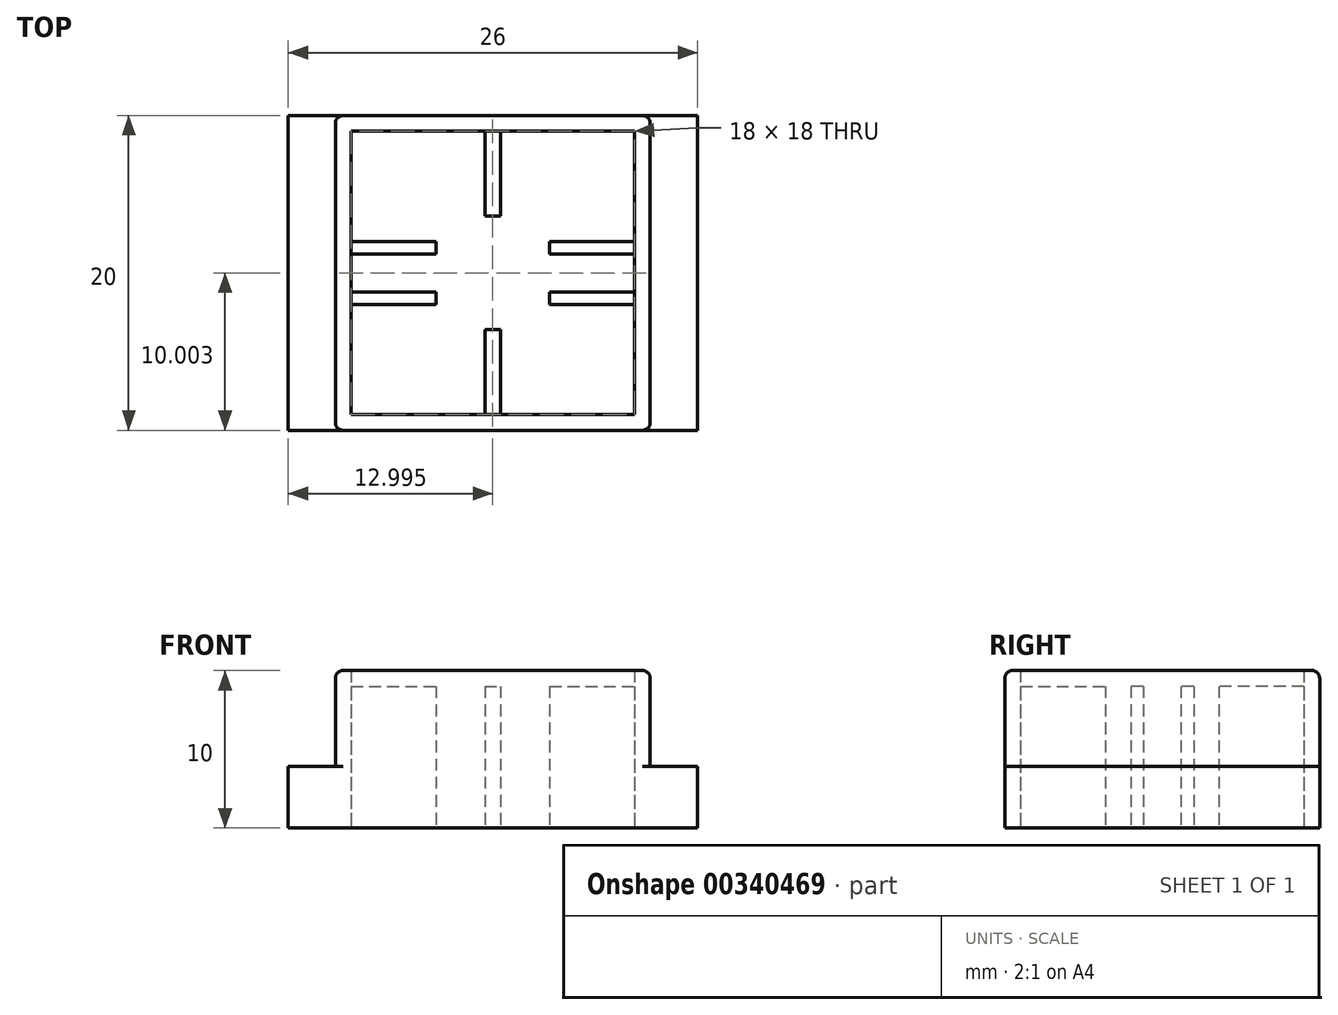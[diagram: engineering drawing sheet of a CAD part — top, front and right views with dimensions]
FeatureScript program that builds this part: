
annotation { "Feature Type Name" : "Feature", "Feature Type Description" : "" }
export const myFeature = defineFeature(function(context is Context, id is Id, definition is map)
    precondition{}
    {
        {
            var Q0;
            Q0=qCreatedBy(makeId("Top.planeOp"),FACE);
            var sketch = newSketch(context, id + "F0", { "sketchPlane" : qUnion([Q0])});
            skLineSegment(sketch, "E0.bottom", {"start": v(-88.88, 8.7) * mm, "end": v(-68.88, 8.7) * mm});
            skLineSegment(sketch, "E0.top", {"start": v(-88.88, -11.3) * mm, "end": v(-68.88, -11.3) * mm});
            skLineSegment(sketch, "E0.left", {"start": v(-88.88, 8.7) * mm, "end": v(-88.88, -11.3) * mm});
            skLineSegment(sketch, "E0.right", {"start": v(-68.88, 8.7) * mm, "end": v(-68.88, -11.3) * mm});
            skSolve(sketch);
        }
        {
            var Q0;
            Q0=makeQuery(id+"F0.imprint","IMPRINT",FACE,{"disambiguationData":[TD([[makeQuery(id+"F0.imprint","IMPRINT",EDGE,{"derivedFrom":sQuery(id+"F0.wireOp",EDGE,"E0.bottom")}),-1.0]])]});
            extrude(context, id + "F1", {"entities" : qUnion([Q0]), "depth" : 10 * mm});
        }
        {
            var Q0;
            Q0=makeQuery(id+"F6.boolean.opBoolean","MERGE",FACE,{"derivedFrom":[makeQuery(id+"F1.opExtrude","CAP_FACE",FACE,{"disambiguationData":[OSD([sQuery(id+"F0.wireOp",EDGE,"E0.bottom"),sQuery(id+"F0.wireOp",EDGE,"E0.top"),sQuery(id+"F0.wireOp",EDGE,"E0.left"),sQuery(id+"F0.wireOp",EDGE,"E0.right")])],"isStart":true}),makeQuery(id+"F6.opExtrude","CAP_FACE",FACE,{"disambiguationData":[OSD([sQuery(id+"F5.wireOp",EDGE,"E8.bottom"),sQuery(id+"F5.wireOp",EDGE,"E8.top"),sQuery(id+"F5.wireOp",EDGE,"E8.left"),sQuery(id+"F5.wireOp",EDGE,"E8.right"),sQuery(id+"F5.wireOp",EDGE,"E9.trimOffspring"),sQuery(id+"F5.wireOp",EDGE,"E11.trimOffspring"),sQuery(id+"F5.wireOp",EDGE,"E13"),sQuery(id+"F5.wireOp",EDGE,"E14"),sQuery(id+"F5.wireOp",EDGE,"E15.bottom"),sQuery(id+"F5.wireOp",EDGE,"E15.top"),sQuery(id+"F5.wireOp",EDGE,"E15.left"),sQuery(id+"F5.wireOp",EDGE,"E16.bottom"),sQuery(id+"F5.wireOp",EDGE,"E16.top"),sQuery(id+"F5.wireOp",EDGE,"E16.left"),sQuery(id+"F5.wireOp",EDGE,"E17.bottom"),sQuery(id+"F5.wireOp",EDGE,"E17.top"),sQuery(id+"F5.wireOp",EDGE,"E17.right"),sQuery(id+"F5.wireOp",EDGE,"E18.bottom"),sQuery(id+"F5.wireOp",EDGE,"E18.top"),sQuery(id+"F5.wireOp",EDGE,"E18.right")])],"isStart":true})]});
            var sketch = newSketch(context, id + "F2", { "sketchPlane" : qUnion([Q0])});
            skLineSegment(sketch, "E1.bottom", {"start": v(-88.88, 11.3) * mm, "end": v(-68.88, 11.3) * mm});
            skLineSegment(sketch, "E1.top", {"start": v(-88.88, 14.3) * mm, "end": v(-68.88, 14.3) * mm, "construction": true});
            skLineSegment(sketch, "E1.left", {"start": v(-88.88, 11.3) * mm, "end": v(-88.88, 14.3) * mm, "construction": true});
            skLineSegment(sketch, "E1.right", {"start": v(-68.88, 11.3) * mm, "end": v(-68.88, 14.3) * mm, "construction": true});
            skLineSegment(sketch, "E2.bottom", {"start": v(-88.88, -8.7) * mm, "end": v(-68.88, -8.7) * mm});
            skLineSegment(sketch, "E2.top", {"start": v(-88.88, -11.7) * mm, "end": v(-68.88, -11.7) * mm});
            skLineSegment(sketch, "E2.left", {"start": v(-88.88, -8.7) * mm, "end": v(-88.88, -11.7) * mm, "construction": true});
            skLineSegment(sketch, "E2.right", {"start": v(-68.88, -8.7) * mm, "end": v(-68.88, -11.7) * mm, "construction": true});
            skLineSegment(sketch, "E3.bottom", {"start": v(-88.88, -8.7) * mm, "end": v(-91.88, -8.7) * mm});
            skLineSegment(sketch, "E3.top", {"start": v(-88.88, 11.3) * mm, "end": v(-91.88, 11.3) * mm});
            skLineSegment(sketch, "E3.left", {"start": v(-88.88, -8.7) * mm, "end": v(-88.88, 11.3) * mm});
            skLineSegment(sketch, "E3.right", {"start": v(-91.88, -8.7) * mm, "end": v(-91.88, 11.3) * mm});
            skLineSegment(sketch, "E4.bottom", {"start": v(-68.88, -8.7) * mm, "end": v(-65.88, -8.7) * mm});
            skLineSegment(sketch, "E4.top", {"start": v(-68.88, 11.3) * mm, "end": v(-65.88, 11.3) * mm});
            skLineSegment(sketch, "E4.left", {"start": v(-68.88, -8.7) * mm, "end": v(-68.88, 11.3) * mm});
            skLineSegment(sketch, "E4.right", {"start": v(-65.88, -8.7) * mm, "end": v(-65.88, 11.3) * mm});
            skLineSegment(sketch, "E5.bottom", {"start": v(-88.88, -11.7) * mm, "end": v(-68.88, -11.7) * mm, "construction": true});
            skLineSegment(sketch, "E5.top", {"start": v(-88.88, -16.7) * mm, "end": v(-68.88, -16.7) * mm, "construction": true});
            skLineSegment(sketch, "E5.left", {"start": v(-88.88, -11.7) * mm, "end": v(-88.88, -16.7) * mm, "construction": true});
            skLineSegment(sketch, "E5.right", {"start": v(-68.88, -11.7) * mm, "end": v(-68.88, -16.7) * mm, "construction": true});
            skCircle(sketch, "E6", {"center": v(-78.88, -13.7) * mm, "radius": 1.5 * mm, "construction": true});
            skSolve(sketch);
        }
        {
            var Q0;
            Q0=qSketchRegion(id+"F2",true);
            extrude(context, id + "F3", {"entities" : qUnion([Q0]), "operationType" : NewBodyOperationType.ADD, "oppositeDirection" : true, "depth" : 0.95 * mm});
        }
        {
            var Q0;
            Q0=makeQuery(id+"F1.opExtrude","CAP_FACE",FACE,{"disambiguationData":[OSD([sQuery(id+"F0.wireOp",EDGE,"E0.bottom"),sQuery(id+"F0.wireOp",EDGE,"E0.top"),sQuery(id+"F0.wireOp",EDGE,"E0.left"),sQuery(id+"F0.wireOp",EDGE,"E0.right")])],"isStart":true});
            shell(context, id + "F4", {"entities" : qUnion([Q0]), "thickness" : 1 * mm});
        }
        {
            var Q0;
            Q0=qCreatedBy(makeId("Top.planeOp"),FACE);
            var sketch = newSketch(context, id + "F5", { "sketchPlane" : qUnion([Q0])});
            skLineSegment(sketch, "E7.bottom", {"start": v(-87.88, -0.1) * mm, "end": v(-79.38, -0.1) * mm, "construction": true});
            skLineSegment(sketch, "E7.top", {"start": v(-87.88, -2.5) * mm, "end": v(-79.38, -2.5) * mm, "construction": true});
            skLineSegment(sketch, "E7.left", {"start": v(-87.88, -0.1) * mm, "end": v(-87.88, -2.5) * mm, "construction": true});
            skLineSegment(sketch, "E7.right", {"start": v(-69.88, -0.1) * mm, "end": v(-69.88, -2.5) * mm, "construction": true});
            skLineSegment(sketch, "E8.bottom", {"start": v(-79.38, 7.7) * mm, "end": v(-78.38, 7.7) * mm});
            skLineSegment(sketch, "E8.top", {"start": v(-79.38, -10.3) * mm, "end": v(-78.38, -10.3) * mm});
            skLineSegment(sketch, "E8.left", {"start": v(-79.38, 7.7) * mm, "end": v(-79.38, -0.1) * mm});
            skLineSegment(sketch, "E8.right", {"start": v(-78.38, 7.7) * mm, "end": v(-78.38, -0.1) * mm});
            skLineSegment(sketch, "E9.trimOffspring", {"start": v(-79.38, -10.3) * mm, "end": v(-79.38, -2.5) * mm});
            skLineSegment(sketch, "E10.trimOffspring", {"start": v(-78.38, -0.1) * mm, "end": v(-69.88, -0.1) * mm, "construction": true});
            skLineSegment(sketch, "E11.trimOffspring", {"start": v(-78.38, -2.5) * mm, "end": v(-78.38, -10.3) * mm});
            skLineSegment(sketch, "E12.trimOffspring", {"start": v(-78.38, -2.5) * mm, "end": v(-69.88, -2.5) * mm, "construction": true});
            skLineSegment(sketch, "E13", {"start": v(-79.38, -2.5) * mm, "end": v(-79.38, -0.1) * mm});
            skLineSegment(sketch, "E14", {"start": v(-78.38, -2.5) * mm, "end": v(-78.38, -0.1) * mm});
            skLineSegment(sketch, "E15.bottom", {"start": v(-87.88, -2.5) * mm, "end": v(-79.38, -2.5) * mm});
            skLineSegment(sketch, "E15.top", {"start": v(-87.88, -3.3) * mm, "end": v(-79.38, -3.3) * mm});
            skLineSegment(sketch, "E15.left", {"start": v(-87.88, -2.5) * mm, "end": v(-87.88, -3.3) * mm});
            skLineSegment(sketch, "E15.right", {"start": v(-79.38, -2.5) * mm, "end": v(-79.38, -3.3) * mm});
            skLineSegment(sketch, "E16.bottom", {"start": v(-87.88, -0.1) * mm, "end": v(-79.38, -0.1) * mm});
            skLineSegment(sketch, "E16.top", {"start": v(-87.88, 0.7) * mm, "end": v(-79.38, 0.7) * mm});
            skLineSegment(sketch, "E16.left", {"start": v(-87.88, -0.1) * mm, "end": v(-87.88, 0.7) * mm});
            skLineSegment(sketch, "E16.right", {"start": v(-79.38, -0.1) * mm, "end": v(-79.38, 0.7) * mm});
            skLineSegment(sketch, "E17.bottom", {"start": v(-78.38, -3.3) * mm, "end": v(-69.88, -3.3) * mm});
            skLineSegment(sketch, "E17.top", {"start": v(-78.38, -2.5) * mm, "end": v(-69.88, -2.5) * mm});
            skLineSegment(sketch, "E17.left", {"start": v(-78.38, -3.3) * mm, "end": v(-78.38, -2.5) * mm});
            skLineSegment(sketch, "E17.right", {"start": v(-69.88, -3.3) * mm, "end": v(-69.88, -2.5) * mm});
            skLineSegment(sketch, "E18.bottom", {"start": v(-78.38, -0.1) * mm, "end": v(-69.88, -0.1) * mm});
            skLineSegment(sketch, "E18.top", {"start": v(-78.38, 0.7) * mm, "end": v(-69.88, 0.7) * mm});
            skLineSegment(sketch, "E18.left", {"start": v(-78.38, -0.1) * mm, "end": v(-78.38, 0.7) * mm});
            skLineSegment(sketch, "E18.right", {"start": v(-69.88, -0.1) * mm, "end": v(-69.88, 0.7) * mm});
            skSolve(sketch);
        }
        {
            var Q0;
            Q0=makeQuery(id+"F5.imprint","IMPRINT",FACE,{"disambiguationData":[TD([[makeQuery(id+"F5.imprint","IMPRINT",EDGE,{"derivedFrom":sQuery(id+"F5.wireOp",EDGE,"E8.bottom")}),-1.0]])]});
            var Q1;
            Q1=makeQuery(id+"F5.imprint","IMPRINT",FACE,{"disambiguationData":[TD([[makeQuery(id+"F5.imprint","IMPRINT",EDGE,{"derivedFrom":sQuery(id+"F5.wireOp",EDGE,"E15.bottom")}),-1.0]])]});
            var Q2;
            Q2=makeQuery(id+"F5.imprint","IMPRINT",FACE,{"disambiguationData":[TD([[makeQuery(id+"F5.imprint","IMPRINT",EDGE,{"derivedFrom":sQuery(id+"F5.wireOp",EDGE,"E16.bottom")}),1.0]])]});
            var Q3;
            Q3=makeQuery(id+"F5.imprint","IMPRINT",FACE,{"disambiguationData":[TD([[makeQuery(id+"F5.imprint","IMPRINT",EDGE,{"derivedFrom":sQuery(id+"F5.wireOp",EDGE,"E18.bottom")}),1.0]])]});
            var Q4;
            Q4=makeQuery(id+"F5.imprint","IMPRINT",FACE,{"disambiguationData":[TD([[makeQuery(id+"F5.imprint","IMPRINT",EDGE,{"derivedFrom":sQuery(id+"F5.wireOp",EDGE,"E17.bottom")}),1.0]])]});
            var Q5;
            Q5=sQuery(id+"F5.wireOp",EDGE,"E8.left");
            var Q6;
            Q6=sQuery(id+"F5.wireOp",EDGE,"E9.trimOffspring");
            var Q7;
            Q7=sQuery(id+"F5.wireOp",EDGE,"E7.top");
            var Q8;
            Q8=sQuery(id+"F5.wireOp",EDGE,"E10.trimOffspring");
            var Q9;
            Q9=sQuery(id+"F5.wireOp",EDGE,"E8.bottom");
            var Q10;
            Q10=sQuery(id+"F5.wireOp",EDGE,"E8.right");
            var Q11;
            Q11=sQuery(id+"F5.wireOp",EDGE,"E8.top");
            var Q12;
            Q12=sQuery(id+"F5.wireOp",EDGE,"E7.bottom");
            var Q13;
            Q13=sQuery(id+"F5.wireOp",EDGE,"E11.trimOffspring");
            var Q14;
            Q14=sQuery(id+"F5.wireOp",EDGE,"E12.trimOffspring");
            var Q15;
            Q15=sQuery(id+"F5.wireOp",EDGE,"E7.right");
            var Q16;
            Q16=sQuery(id+"F5.wireOp",EDGE,"E7.left");
            extrude(context, id + "F6", {"entities" : qUnion([Q0, Q1, Q2, Q3, Q4]), "operationType" : NewBodyOperationType.ADD, "surfaceEntities" : qUnion([Q5, Q6, Q7, Q8, Q9, Q10, Q11, Q12, Q13, Q14, Q15, Q16]), "depth" : 9 * mm});
        }
        {
            var Q0;
            Q0=makeQuery(id+"F6.boolean.opBoolean","MERGE",FACE,{"derivedFrom":[makeQuery(id+"F1.opExtrude","CAP_FACE",FACE,{"disambiguationData":[OSD([sQuery(id+"F0.wireOp",EDGE,"E0.bottom"),sQuery(id+"F0.wireOp",EDGE,"E0.top"),sQuery(id+"F0.wireOp",EDGE,"E0.left"),sQuery(id+"F0.wireOp",EDGE,"E0.right")])],"isStart":true}),makeQuery(id+"F6.opExtrude","CAP_FACE",FACE,{"disambiguationData":[OSD([sQuery(id+"F5.wireOp",EDGE,"E7.bottom"),sQuery(id+"F5.wireOp",EDGE,"E7.top"),sQuery(id+"F5.wireOp",EDGE,"E7.left"),sQuery(id+"F5.wireOp",EDGE,"E7.right"),sQuery(id+"F5.wireOp",EDGE,"E8.bottom"),sQuery(id+"F5.wireOp",EDGE,"E8.top"),sQuery(id+"F5.wireOp",EDGE,"E8.left"),sQuery(id+"F5.wireOp",EDGE,"E8.right"),sQuery(id+"F5.wireOp",EDGE,"E9.trimOffspring"),sQuery(id+"F5.wireOp",EDGE,"E10.trimOffspring"),sQuery(id+"F5.wireOp",EDGE,"E11.trimOffspring"),sQuery(id+"F5.wireOp",EDGE,"E12.trimOffspring")])],"isStart":true})]});
            var sketch = newSketch(context, id + "F7", { "sketchPlane" : qUnion([Q0])});
            skLineSegment(sketch, "E19.bottom", {"start": v(-75.28, -2.3) * mm, "end": v(-82.48, -2.3) * mm});
            skLineSegment(sketch, "E19.top", {"start": v(-75.28, 4.9) * mm, "end": v(-82.48, 4.9) * mm});
            skLineSegment(sketch, "E19.left", {"start": v(-75.28, -2.3) * mm, "end": v(-75.28, 4.9) * mm});
            skLineSegment(sketch, "E19.right", {"start": v(-82.48, -2.3) * mm, "end": v(-82.48, 4.9) * mm});
            skPoint(sketch, "E19.middle.positionSnap1", {"position": v(-88.88, 1.8) * mm});
            skSolve(sketch);
        }
        {
            var Q0;
            {var subQ1=makeQuery(id+"F6.opExtrude","CAP_EDGE",EDGE,{"disambiguationData":[OSD([sQuery(id+"F5.wireOp",EDGE,"E8.right")])],"isStart":true});var subQ3=sQuery(id+"F7.wireOp",EDGE,"E19.bottom");var subQ4=makeQuery(id+"F7.imprint","INTERSECT",VERTEX,{"derivedFrom":[subQ1,subQ3]});Q0=makeQuery(id+"F7.imprint","IMPRINT",FACE,{"disambiguationData":[TD([[makeQuery(id+"F7.imprint","IMPRINT",EDGE,{"disambiguationData":[TD([[subQ4,-1.0]])],"derivedFrom":subQ3}),-1.0]])]});}
            extrude(context, id + "F8", {"entities" : qUnion([Q0]), "operationType" : NewBodyOperationType.REMOVE, "oppositeDirection" : true, "depth" : 9 * mm});
        }
        {
            var Q0;
            Q0=makeQuery(id+"F1.opExtrude","SWEPT_EDGE",EDGE,{"disambiguationData":[OSD([sQuery(id+"F0.wireOp",EDGE,"E0.top"),sQuery(id+"F0.wireOp",EDGE,"E0.right")])]});
            var Q1;
            Q1=makeQuery(id+"F1.opExtrude","CAP_EDGE",EDGE,{"disambiguationData":[OSD([sQuery(id+"F0.wireOp",EDGE,"E0.top")])],"isStart":false});
            var Q2;
            Q2=makeQuery(id+"F1.opExtrude","CAP_EDGE",EDGE,{"disambiguationData":[OSD([sQuery(id+"F0.wireOp",EDGE,"E0.right")])],"isStart":false});
            var Q3;
            Q3=makeQuery(id+"F1.opExtrude","SWEPT_EDGE",EDGE,{"disambiguationData":[OSD([sQuery(id+"F0.wireOp",EDGE,"E0.bottom"),sQuery(id+"F0.wireOp",EDGE,"E0.right")])]});
            var Q4;
            Q4=makeQuery(id+"F1.opExtrude","CAP_EDGE",EDGE,{"disambiguationData":[OSD([sQuery(id+"F0.wireOp",EDGE,"E0.bottom")])],"isStart":false});
            var Q5;
            Q5=makeQuery(id+"F1.opExtrude","SWEPT_EDGE",EDGE,{"disambiguationData":[OSD([sQuery(id+"F0.wireOp",EDGE,"E0.bottom"),sQuery(id+"F0.wireOp",EDGE,"E0.left")])]});
            var Q6;
            Q6=makeQuery(id+"F1.opExtrude","CAP_EDGE",EDGE,{"disambiguationData":[OSD([sQuery(id+"F0.wireOp",EDGE,"E0.left")])],"isStart":false});
            var Q7;
            Q7=makeQuery(id+"F1.opExtrude","SWEPT_EDGE",EDGE,{"disambiguationData":[OSD([sQuery(id+"F0.wireOp",EDGE,"E0.top"),sQuery(id+"F0.wireOp",EDGE,"E0.left")])]});
            var Q8;
            Q8=makeQuery(id+"FdcNGCSEVtLFmFF_0.opExtrude","SWEPT_EDGE",EDGE,{"disambiguationData":[OSD([sQuery(id+"FRnwog6KuLiXbKg_0.wireOp",EDGE,"NmKWu525-oT8c-AXwx-9Qw7-ty39SNDPMHe7.bottom"),sQuery(id+"FRnwog6KuLiXbKg_0.wireOp",EDGE,"NmKWu525-oT8c-AXwx-9Qw7-ty39SNDPMHe7.right")])]});
            var Q9;
            Q9=makeQuery(id+"FdcNGCSEVtLFmFF_0.opExtrude","CAP_EDGE",EDGE,{"disambiguationData":[OSD([sQuery(id+"FRnwog6KuLiXbKg_0.wireOp",EDGE,"NmKWu525-oT8c-AXwx-9Qw7-ty39SNDPMHe7.bottom")])],"isStart":false});
            var Q10;
            Q10=makeQuery(id+"FdcNGCSEVtLFmFF_0.opExtrude","SWEPT_EDGE",EDGE,{"disambiguationData":[OSD([sQuery(id+"FRnwog6KuLiXbKg_0.wireOp",EDGE,"NmKWu525-oT8c-AXwx-9Qw7-ty39SNDPMHe7.bottom"),sQuery(id+"FRnwog6KuLiXbKg_0.wireOp",EDGE,"NmKWu525-oT8c-AXwx-9Qw7-ty39SNDPMHe7.left")])]});
            var Q11;
            Q11=makeQuery(id+"FdcNGCSEVtLFmFF_0.opExtrude","CAP_EDGE",EDGE,{"disambiguationData":[OSD([sQuery(id+"FRnwog6KuLiXbKg_0.wireOp",EDGE,"NmKWu525-oT8c-AXwx-9Qw7-ty39SNDPMHe7.right")])],"isStart":false});
            var Q12;
            Q12=makeQuery(id+"FdcNGCSEVtLFmFF_0.opExtrude","SWEPT_EDGE",EDGE,{"disambiguationData":[OSD([sQuery(id+"FRnwog6KuLiXbKg_0.wireOp",EDGE,"NmKWu525-oT8c-AXwx-9Qw7-ty39SNDPMHe7.top"),sQuery(id+"FRnwog6KuLiXbKg_0.wireOp",EDGE,"NmKWu525-oT8c-AXwx-9Qw7-ty39SNDPMHe7.right")])]});
            var Q13;
            Q13=makeQuery(id+"FdcNGCSEVtLFmFF_0.opExtrude","CAP_EDGE",EDGE,{"disambiguationData":[OSD([sQuery(id+"FRnwog6KuLiXbKg_0.wireOp",EDGE,"NmKWu525-oT8c-AXwx-9Qw7-ty39SNDPMHe7.top")])],"isStart":false});
            var Q14;
            Q14=makeQuery(id+"FdcNGCSEVtLFmFF_0.opExtrude","SWEPT_EDGE",EDGE,{"disambiguationData":[OSD([sQuery(id+"FRnwog6KuLiXbKg_0.wireOp",EDGE,"NmKWu525-oT8c-AXwx-9Qw7-ty39SNDPMHe7.top"),sQuery(id+"FRnwog6KuLiXbKg_0.wireOp",EDGE,"NmKWu525-oT8c-AXwx-9Qw7-ty39SNDPMHe7.left")])]});
            var Q15;
            Q15=makeQuery(id+"FdcNGCSEVtLFmFF_0.opExtrude","CAP_EDGE",EDGE,{"disambiguationData":[OSD([sQuery(id+"FRnwog6KuLiXbKg_0.wireOp",EDGE,"NmKWu525-oT8c-AXwx-9Qw7-ty39SNDPMHe7.left")])],"isStart":false});
            fillet(context, id + "F9", {"entities" : qUnion([Q0, Q1, Q2, Q3, Q4, Q5, Q6, Q7, Q8, Q9, Q10, Q11, Q12, Q13, Q14, Q15]), "radius" : 0.5 * mm, "tangentPropagation" : true, "allowEdgeOverflow" : false});
        }
        {
            var Q0;
            {var subQ1=sQuery(id+"F2.wireOp",EDGE,"E5.bottom");var subQ2=sQuery(id+"F2.wireOp",EDGE,"E4.right");var subQ3=sQuery(id+"F2.wireOp",EDGE,"E4.top");var subQ4=sQuery(id+"F2.wireOp",EDGE,"E4.bottom");var subQ5=sQuery(id+"F2.wireOp",EDGE,"E3.right");var subQ6=sQuery(id+"F2.wireOp",EDGE,"E3.top");var subQ7=sQuery(id+"F2.wireOp",EDGE,"E3.bottom");var subQ8=sQuery(id+"F2.wireOp",EDGE,"E2.right");var subQ9=sQuery(id+"F2.wireOp",EDGE,"E2.left");var subQ10=sQuery(id+"F2.wireOp",EDGE,"E1.right");var subQ11=sQuery(id+"F2.wireOp",EDGE,"E1.left");var subQ12=sQuery(id+"F2.wireOp",EDGE,"E1.top");var subQ13=makeQuery(id+"F3.opExtrude","CAP_FACE",FACE,{"disambiguationData":[OSD([subQ12,subQ11,subQ10,subQ9,subQ8,subQ7,subQ6,subQ5,subQ4,subQ3,subQ2,subQ1])],"isStart":false});Q0=makeQuery(id+"F9.opFillet","MERGE",FACE,{"derivedFrom":[makeQuery(id+"F3.boolean.opBoolean","SPLIT",FACE,{"disambiguationData":[TD([makeQuery(id+"F3.opExtrude","SWEPT_FACE",FACE,{"disambiguationData":[OSD([subQ12])]})])],"derivedFrom":subQ13}),makeQuery(id+"F3.boolean.opBoolean","SPLIT",FACE,{"disambiguationData":[TD([makeQuery(id+"F3.opExtrude","SWEPT_FACE",FACE,{"disambiguationData":[OSD([subQ1])]})])],"derivedFrom":subQ13}),makeQuery(id+"F3.boolean.opBoolean","SPLIT",FACE,{"disambiguationData":[TD([makeQuery(id+"F3.opExtrude","SWEPT_FACE",FACE,{"disambiguationData":[OSD([subQ5])]})])],"derivedFrom":subQ13}),makeQuery(id+"F3.boolean.opBoolean","SPLIT",FACE,{"disambiguationData":[TD([makeQuery(id+"F3.opExtrude","SWEPT_FACE",FACE,{"disambiguationData":[OSD([subQ2])]})])],"derivedFrom":subQ13})]});}
            extrude(context, id + "F10", {"entities" : qUnion([Q0]), "operationType" : NewBodyOperationType.ADD, "depth" : 0.05 * mm});
        }
        {
            var Q0;
            Q0=makeQuery(id+"F1.opExtrude","CAP_FACE",FACE,{"disambiguationData":[OSD([sQuery(id+"F0.wireOp",EDGE,"E0.bottom"),sQuery(id+"F0.wireOp",EDGE,"E0.top"),sQuery(id+"F0.wireOp",EDGE,"E0.left"),sQuery(id+"F0.wireOp",EDGE,"E0.right")])],"isStart":false});
            var sketch = newSketch(context, id + "F11", { "sketchPlane" : qUnion([Q0])});
            skLineSegment(sketch, "E20.bottom", {"start": v(-87.88, 7.7) * mm, "end": v(-69.88, 7.7) * mm});
            skLineSegment(sketch, "E20.top", {"start": v(-87.88, -10.3) * mm, "end": v(-69.88, -10.3) * mm});
            skLineSegment(sketch, "E20.left", {"start": v(-87.88, 7.7) * mm, "end": v(-87.88, -10.3) * mm});
            skLineSegment(sketch, "E20.right", {"start": v(-69.88, 7.7) * mm, "end": v(-69.88, -10.3) * mm});
            skSolve(sketch);
        }
        {
            var Q0;
            Q0=qSketchRegion(id+"F11",true);
            extrude(context, id + "F12", {"entities" : qUnion([Q0]), "operationType" : NewBodyOperationType.REMOVE, "oppositeDirection" : true, "depth" : 1 * mm});
        }
        {
            var Q0;
            {var subQ0=sQuery(id+"F2.wireOp",EDGE,"E4.bottom");var subQ1=sQuery(id+"F2.wireOp",EDGE,"E3.bottom");var subQ2=sQuery(id+"F2.wireOp",EDGE,"E2.bottom");var subQ3=sQuery(id+"F2.wireOp",EDGE,"E4.top");var subQ4=sQuery(id+"F2.wireOp",EDGE,"E3.top");var subQ5=sQuery(id+"F2.wireOp",EDGE,"E1.bottom");var subQ6=sQuery(id+"F2.wireOp",EDGE,"E3.right");var subQ7=sQuery(id+"F2.wireOp",EDGE,"E4.right");Q0=makeQuery(id+"F10.opExtrude","CAP_FACE",FACE,{"disambiguationData":[OSD([subQ5,subQ2,subQ1,subQ4,subQ6,subQ0,subQ3,subQ7]),TDD([makeQuery(id+"F3.boolean.opBoolean","SPLIT",FACE,{"disambiguationData":[TD([makeQuery(id+"F1.opExtrude","SWEPT_FACE",FACE,{"disambiguationData":[OSD([sQuery(id+"F0.wireOp",EDGE,"E0.left")])]})])],"derivedFrom":makeQuery(id+"F3.opExtrude","CAP_FACE",FACE,{"disambiguationData":[OSD([subQ5,subQ2,subQ1,subQ4,subQ6,subQ0,subQ3,subQ7])],"isStart":false})})])],"isStart":false});}
            var Q1;
            {var subQ0=sQuery(id+"F2.wireOp",EDGE,"E4.top");var subQ1=sQuery(id+"F2.wireOp",EDGE,"E3.top");var subQ2=sQuery(id+"F2.wireOp",EDGE,"E1.bottom");var subQ3=sQuery(id+"F2.wireOp",EDGE,"E4.bottom");var subQ4=sQuery(id+"F2.wireOp",EDGE,"E3.bottom");var subQ5=sQuery(id+"F2.wireOp",EDGE,"E2.bottom");var subQ6=sQuery(id+"F2.wireOp",EDGE,"E4.right");var subQ7=sQuery(id+"F2.wireOp",EDGE,"E3.right");Q1=makeQuery(id+"F10.opExtrude","CAP_FACE",FACE,{"disambiguationData":[OSD([subQ2,subQ5,subQ4,subQ1,subQ7,subQ3,subQ0,subQ6]),TDD([makeQuery(id+"F3.boolean.opBoolean","SPLIT",FACE,{"disambiguationData":[TD([makeQuery(id+"F1.opExtrude","SWEPT_FACE",FACE,{"disambiguationData":[OSD([sQuery(id+"F0.wireOp",EDGE,"E0.right")])]})])],"derivedFrom":makeQuery(id+"F3.opExtrude","CAP_FACE",FACE,{"disambiguationData":[OSD([subQ2,subQ5,subQ4,subQ1,subQ7,subQ3,subQ0,subQ6])],"isStart":false})})])],"isStart":false});}
            extrude(context, id + "F13", {"entities" : qUnion([Q0, Q1]), "operationType" : NewBodyOperationType.ADD, "depth" : 2.9 * mm});
        }
    });
